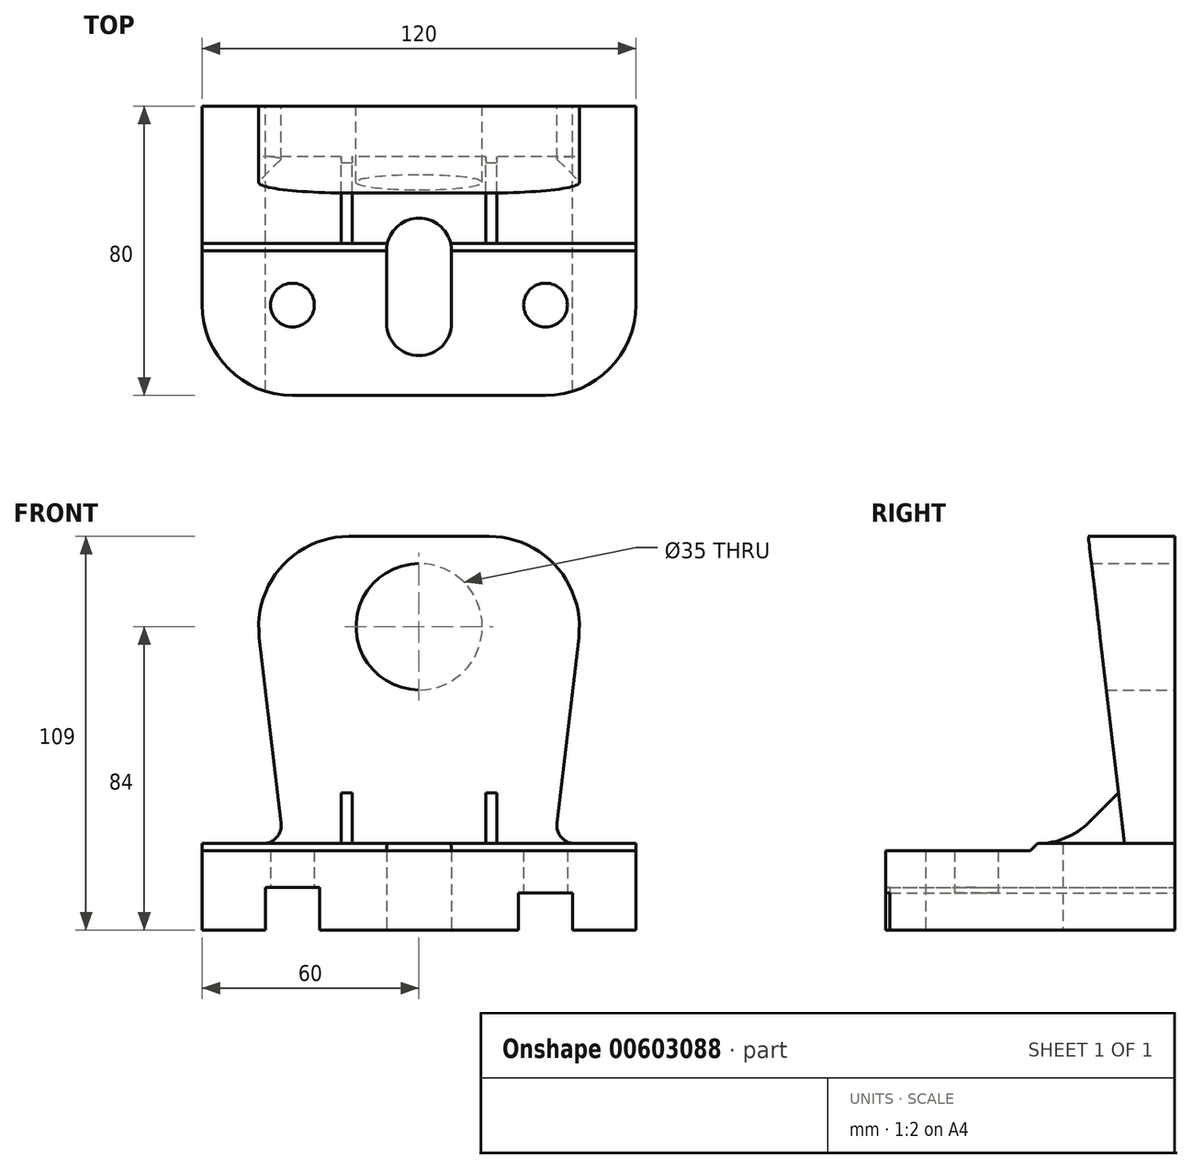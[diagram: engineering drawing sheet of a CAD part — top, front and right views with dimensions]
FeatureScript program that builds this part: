
annotation { "Feature Type Name" : "Feature", "Feature Type Description" : "" }
export const myFeature = defineFeature(function(context is Context, id is Id, definition is map)
    precondition{}
    {
        {
            var Q0;
            Q0=qCreatedBy(makeId("Right.planeOp"),FACE);
            var sketch = newSketch(context, id + "F0", { "sketchPlane" : qUnion([Q0])});
            skLineSegment(sketch, "E0", {"start": v(0, 0) * mm, "end": v(0, 109) * mm});
            skLineSegment(sketch, "E1", {"start": v(0, 109) * mm, "end": v(-24, 109) * mm});
            skLineSegment(sketch, "E2", {"start": v(-24, 109) * mm, "end": v(-14, 24) * mm});
            skLineSegment(sketch, "E3", {"start": v(-14, 24) * mm, "end": v(-40, 24) * mm});
            skLineSegment(sketch, "E4", {"start": v(-40, 24) * mm, "end": v(-40, 22) * mm});
            skLineSegment(sketch, "E5", {"start": v(-40, 22) * mm, "end": v(-80, 22) * mm});
            skLineSegment(sketch, "E6", {"start": v(-80, 22) * mm, "end": v(-80, 0) * mm});
            skLineSegment(sketch, "E7", {"start": v(-80, 0) * mm, "end": v(0, 0) * mm});
            skSolve(sketch);
        }
        {
            var Q0;
            Q0 = qSketchRegion(id + "F0", true);
            extrude(context, id + "F1", {"entities" : qUnion([Q0]), "endBound" : BoundingType.SYMMETRIC, "depth" : 120 * mm, "offsetDistance" : 25 * mm});
        }
        {
            var Q0;
            Q0=qCreatedBy(makeId("Front.planeOp"),FACE);
            var sketch = newSketch(context, id + "F2", { "sketchPlane" : qUnion([Q0])});
            skLineSegment(sketch, "E8", {"start": v(-35, 0) * mm, "end": v(-35, 109) * mm, "construction": true});
            skLineSegment(sketch, "E9", {"start": v(35, 0) * mm, "end": v(35, 109) * mm, "construction": true});
            skLineSegment(sketch, "E10.bottom", {"start": v(-42.5, 0) * mm, "end": v(-27.5, 0) * mm});
            skLineSegment(sketch, "E10.top", {"start": v(-42.5, 11.9) * mm, "end": v(-27.5, 11.9) * mm});
            skLineSegment(sketch, "E10.left", {"start": v(-42.5, 0) * mm, "end": v(-42.5, 11.9) * mm});
            skLineSegment(sketch, "E10.right", {"start": v(-27.5, 0) * mm, "end": v(-27.5, 11.9) * mm});
            skLineSegment(sketch, "E11.bottom", {"start": v(42.5, 0) * mm, "end": v(27.5, 0) * mm});
            skLineSegment(sketch, "E11.top", {"start": v(42.5, 10.38) * mm, "end": v(27.5, 10.38) * mm});
            skLineSegment(sketch, "E11.left", {"start": v(42.5, 0) * mm, "end": v(42.5, 10.38) * mm});
            skLineSegment(sketch, "E11.right", {"start": v(27.5, 0) * mm, "end": v(27.5, 10.38) * mm});
            skSolve(sketch);
        }
        {
            var Q0;
            Q0 = qSketchRegion(id + "F2", true);
            extrude(context, id + "F3", {"entities" : qUnion([Q0]), "operationType" : NewBodyOperationType.REMOVE, "endBound" : BoundingType.THROUGH_ALL, "depth" : 25 * mm, "offsetDistance" : 25 * mm});
        }
        {
            var Q0;
            Q0=qCreatedBy(makeId("Front.planeOp"),FACE);
            var sketch = newSketch(context, id + "F4", { "sketchPlane" : qUnion([Q0])});
            skLineSegment(sketch, "E12", {"start": v(0, 0) * mm, "end": v(0, 109) * mm, "construction": true});
            skLineSegment(sketch, "E13", {"start": v(-38.16, 29.58) * mm, "end": v(-44.22, 81.08) * mm});
            skLineSegment(sketch, "E14", {"start": v(-19.39, 109) * mm, "end": v(0, 109) * mm});
            skPoint(sketch, "E15.visualSharp", {"position": v(-47.5, 109) * mm});
            skArc(sketch, "E15.filletArc", {"start": v(-19.39, 109) * mm, "mid": v(-38.07, 100.61) * mm, "end": v(-44.22, 81.08) * mm});
            skLineSegment(sketch, "E16", {"start": v(-43.12, 24) * mm, "end": v(-60, 24) * mm});
            skPoint(sketch, "E17.visualSharp", {"position": v(-37.5, 24) * mm});
            skArc(sketch, "E17.filletArc", {"start": v(-43.12, 24) * mm, "mid": v(-39.39, 25.68) * mm, "end": v(-38.16, 29.58) * mm});
            skArc(sketch, "E18.MirrorCS", {"start": v(43.12, 24) * mm, "mid": v(39.39, 25.68) * mm, "end": v(38.16, 29.58) * mm});
            skPoint(sketch, "E19.MirrorP", {"position": v(47.5, 109) * mm});
            skPoint(sketch, "E20.MirrorP", {"position": v(37.5, 24) * mm});
            skLineSegment(sketch, "E21.MirrorCS", {"start": v(19.39, 109) * mm, "end": v(0, 109) * mm});
            skLineSegment(sketch, "E22.MirrorCS", {"start": v(38.16, 29.58) * mm, "end": v(44.22, 81.08) * mm});
            skLineSegment(sketch, "E23.MirrorCS", {"start": v(43.12, 24) * mm, "end": v(60, 24) * mm});
            skArc(sketch, "E24.MirrorCS", {"start": v(19.39, 109) * mm, "mid": v(38.07, 100.61) * mm, "end": v(44.22, 81.08) * mm});
            skLineSegment(sketch, "E25", {"start": v(-60, 24) * mm, "end": v(-60, 136.87) * mm});
            skLineSegment(sketch, "E26", {"start": v(-60, 136.87) * mm, "end": v(60, 136.87) * mm});
            skLineSegment(sketch, "E27", {"start": v(60, 24) * mm, "end": v(60, 136.87) * mm});
            skSolve(sketch);
        }
        {
            var Q0;
            Q0 = qSketchRegion(id + "F4", true);
            extrude(context, id + "F5", {"entities" : qUnion([Q0]), "operationType" : NewBodyOperationType.REMOVE, "endBound" : BoundingType.THROUGH_ALL, "depth" : 25 * mm, "offsetDistance" : 25 * mm});
        }
        {
            var Q0;
            Q0=qCreatedBy(makeId("Front.planeOp"),FACE);
            var sketch = newSketch(context, id + "F6", { "sketchPlane" : qUnion([Q0])});
            skLineSegment(sketch, "E28", {"start": v(-20, 0) * mm, "end": v(-20, 109) * mm, "construction": true});
            skLineSegment(sketch, "E29", {"start": v(20, 0) * mm, "end": v(20, 109) * mm, "construction": true});
            skLineSegment(sketch, "E30.bottom", {"start": v(-18.5, 24) * mm, "end": v(-21.5, 24) * mm});
            skLineSegment(sketch, "E30.top", {"start": v(-18.5, 39) * mm, "end": v(-21.5, 39) * mm});
            skLineSegment(sketch, "E30.left", {"start": v(-18.5, 24) * mm, "end": v(-18.5, 39) * mm});
            skLineSegment(sketch, "E30.right", {"start": v(-21.5, 24) * mm, "end": v(-21.5, 39) * mm});
            skLineSegment(sketch, "E31.bottom", {"start": v(21.5, 24) * mm, "end": v(18.5, 24) * mm});
            skLineSegment(sketch, "E31.top", {"start": v(21.5, 39) * mm, "end": v(18.5, 39) * mm});
            skLineSegment(sketch, "E31.left", {"start": v(21.5, 24) * mm, "end": v(21.5, 39) * mm});
            skLineSegment(sketch, "E31.right", {"start": v(18.5, 24) * mm, "end": v(18.5, 39) * mm});
            skSolve(sketch);
        }
        {
            var Q0;
            Q0 = qSketchRegion(id + "F6", true);
            var Q1;
            Q1=makeQuery(id+"F1.opExtrude","SWEPT_FACE",FACE,{"disambiguationData":[OSD([sQuery(id+"F0.wireOp",EDGE,"E4")])]});
            extrude(context, id + "F7", {"entities" : qUnion([Q0]), "operationType" : NewBodyOperationType.ADD, "endBound" : BoundingType.UP_TO_SURFACE, "depth" : 25 * mm, "endBoundEntityFace" : qUnion([Q1]), "offsetDistance" : 25 * mm});
        }
        {
            var Q0;
            Q0=qCreatedBy(makeId("Right.planeOp"),FACE);
            var sketch = newSketch(context, id + "F8", { "sketchPlane" : qUnion([Q0])});
            skLineSegment(sketch, "E32", {"start": v(-38, 0) * mm, "end": v(-38, 50) * mm, "construction": true});
            skLineSegment(sketch, "E33", {"start": v(-15.65, 38.06) * mm, "end": v(-23.86, 29.86) * mm});
            skLineSegment(sketch, "E34", {"start": v(-38, 24) * mm, "end": v(-44, 24) * mm});
            skPoint(sketch, "E35.visualSharp", {"position": v(-29.72, 24) * mm});
            skArc(sketch, "E35.filletArc", {"start": v(-38, 24) * mm, "mid": v(-30.35, 25.52) * mm, "end": v(-23.86, 29.86) * mm});
            skLineSegment(sketch, "E36", {"start": v(-15.65, 38.06) * mm, "end": v(-16.33, 43.79) * mm});
            skLineSegment(sketch, "E37", {"start": v(-16.33, 43.79) * mm, "end": v(-44, 43.79) * mm});
            skLineSegment(sketch, "E38", {"start": v(-44, 43.79) * mm, "end": v(-44, 24) * mm});
            skSolve(sketch);
        }
        {
            var Q0;
            Q0 = qSketchRegion(id + "F8", true);
            extrude(context, id + "F9", {"entities" : qUnion([Q0]), "operationType" : NewBodyOperationType.REMOVE, "endBound" : BoundingType.THROUGH_ALL, "oppositeDirection" : true, "depth" : 25 * mm, "offsetDistance" : 25 * mm, "hasSecondDirection" : true, "secondDirectionBound" : SecondDirectionBoundingType.THROUGH_ALL, "secondDirectionOppositeDirection" : false, "secondDirectionDepth" : 25 * mm});
        }
        {
            var Q0;
            Q0=qCreatedBy(makeId("Top.planeOp"),FACE);
            var sketch = newSketch(context, id + "F10", { "sketchPlane" : qUnion([Q0])});
            skCircle(sketch, "E39", {"center": v(-35, -55) * mm, "radius": 7 * mm});
            skCircle(sketch, "E40.MirrorC", {"center": v(35, -55) * mm, "radius": 7 * mm});
            skSolve(sketch);
        }
        {
            var Q0;
            Q0=sQuery(id+"F10.wireOp",VERTEX,"E39.center");
            var Q1;
            Q1=sQuery(id+"F10.wireOp",VERTEX,"E40.MirrorC.center");
            var Q2;
            Q2=makeQuery(id+"F1.opExtrude","SWEPT_BODY",BODY,{"disambiguationData":[OSD([sQuery(id+"F0.wireOp",EDGE,"E0"),sQuery(id+"F0.wireOp",EDGE,"E1"),sQuery(id+"F0.wireOp",EDGE,"E2"),sQuery(id+"F0.wireOp",EDGE,"E3"),sQuery(id+"F0.wireOp",EDGE,"E4"),sQuery(id+"F0.wireOp",EDGE,"E5"),sQuery(id+"F0.wireOp",EDGE,"E6"),sQuery(id+"F0.wireOp",EDGE,"E7")])]});
            hole(context, id + "F11", {"style" : HoleStyle.SIMPLE, "endStyle" : HoleEndStyle.THROUGH, "oppositeDirection" : true, "standardTappedOrClearance" : lookupTablePath({ "standard" : "ISO", "engagement" : "75%", "pitch" : "2 mm", "size" : "M14", "type" : "Tapped" }), "standardBlindInLast" : lookupTablePath({ "standard" : "ISO", "engagement" : "75%", "pitch" : "2 mm", "size" : "M14", "type" : "Tapped" }), "holeDiameter" : 12.1 * mm, "majorDiameter" : 14 * mm, "showTappedDepth" : true, "isTappedThrough" : true, "tappedDepth" : 12 * mm, "tapClearance" : 3, "startFromSketch" : true, "locations" : qUnion([Q0, Q1]), "scope" : qUnion([Q2])});
        }
        {
            var Q0;
            Q0=qCreatedBy(makeId("Top.planeOp"),FACE);
            var sketch = newSketch(context, id + "F12", { "sketchPlane" : qUnion([Q0])});
            skArc(sketch, "E41", {"start": v(-9, -60) * mm, "mid": v(0, -69) * mm, "end": v(9, -60) * mm});
            skArc(sketch, "E42", {"start": v(9, -40) * mm, "mid": v(0, -31) * mm, "end": v(-9, -40) * mm});
            skLineSegment(sketch, "E43", {"start": v(-9, -60) * mm, "end": v(-9, -40) * mm});
            skLineSegment(sketch, "E44", {"start": v(9, -40) * mm, "end": v(9, -60) * mm});
            skSolve(sketch);
        }
        {
            var Q0;
            Q0 = qSketchRegion(id + "F12", true);
            extrude(context, id + "F13", {"entities" : qUnion([Q0]), "operationType" : NewBodyOperationType.REMOVE, "endBound" : BoundingType.THROUGH_ALL, "depth" : 25 * mm, "offsetDistance" : 25 * mm});
        }
        {
            var Q0;
            Q0=qCreatedBy(makeId("Front.planeOp"),FACE);
            var sketch = newSketch(context, id + "F14", { "sketchPlane" : qUnion([Q0])});
            skCircle(sketch, "E45", {"center": v(0, 84) * mm, "radius": 17.5 * mm});
            skSolve(sketch);
        }
        {
            var Q0;
            Q0=sQuery(id+"F14.wireOp",VERTEX,"E45.center");
            var Q1;
            Q1=makeQuery(id+"F1.opExtrude","SWEPT_BODY",BODY,{"disambiguationData":[OSD([sQuery(id+"F0.wireOp",EDGE,"E0"),sQuery(id+"F0.wireOp",EDGE,"E1"),sQuery(id+"F0.wireOp",EDGE,"E2"),sQuery(id+"F0.wireOp",EDGE,"E3"),sQuery(id+"F0.wireOp",EDGE,"E4"),sQuery(id+"F0.wireOp",EDGE,"E5"),sQuery(id+"F0.wireOp",EDGE,"E6"),sQuery(id+"F0.wireOp",EDGE,"E7")])]});
            hole(context, id + "F15", {"style" : HoleStyle.SIMPLE, "endStyle" : HoleEndStyle.THROUGH, "oppositeDirection" : true, "holeDiameter" : 35 * mm, "majorDiameter" : 14 * mm, "isTappedThrough" : true, "tappedDepth" : 12 * mm, "tapClearance" : 3, "startFromSketch" : true, "locations" : qUnion([Q0]), "scope" : qUnion([Q1])});
        }
        {
            var Q0;
            Q0=makeQuery(id+"F1.opExtrude","CAP_EDGE",EDGE,{"disambiguationData":[OSD([sQuery(id+"F0.wireOp",EDGE,"E6")])],"isStart":true});
            var Q1;
            Q1=makeQuery(id+"F1.opExtrude","CAP_EDGE",EDGE,{"disambiguationData":[OSD([sQuery(id+"F0.wireOp",EDGE,"E6")])],"isStart":false});
            fillet(context, id + "F16", {"entities" : qUnion([Q0, Q1]), "radius" : 25 * mm, "tangentPropagation" : true, "allowEdgeOverflow" : false});
        }
        {
            var Q0;
            {var subQ0=makeQuery(id+"F5.opExtrude","SWEPT_FACE",FACE,{"disambiguationData":[OSD([sQuery(id+"F4.wireOp",EDGE,"E23.MirrorCS")])]});var subQ1=makeQuery(id+"F5.opExtrude","SWEPT_FACE",FACE,{"disambiguationData":[OSD([sQuery(id+"F4.wireOp",EDGE,"E16")])]});var subQ8=makeQuery(id+"F5.boolean.opBoolean","INTERSECT",EDGE,{"derivedFrom":[subQ1,subQ0]});Q0=makeQuery(id+"F9.boolean.opBoolean","MERGE",EDGE,{"derivedFrom":[makeQuery(id+"F7.boolean.opBoolean","SPLIT",EDGE,{"disambiguationData":[TD([makeQuery(id+"F7.opExtrude","SWEPT_FACE",FACE,{"disambiguationData":[OSD([sQuery(id+"F6.wireOp",EDGE,"E30.right")])]})])],"derivedFrom":subQ8}),makeQuery(id+"F7.boolean.opBoolean","SPLIT",EDGE,{"disambiguationData":[TD([makeQuery(id+"F7.opExtrude","SWEPT_FACE",FACE,{"disambiguationData":[OSD([sQuery(id+"F6.wireOp",EDGE,"E31.left")])]})])],"derivedFrom":subQ8}),makeQuery(id+"F7.boolean.opBoolean","SPLIT",EDGE,{"disambiguationData":[TD([makeQuery(id+"F7.opExtrude","SWEPT_FACE",FACE,{"disambiguationData":[OSD([sQuery(id+"F6.wireOp",EDGE,"E30.left")])]})])],"derivedFrom":subQ8})]});}
            chamfer(context, id + "F17", {"entities" : qUnion([Q0]), "width" : 2 * mm, "tangentPropagation" : true});
        }
    });
